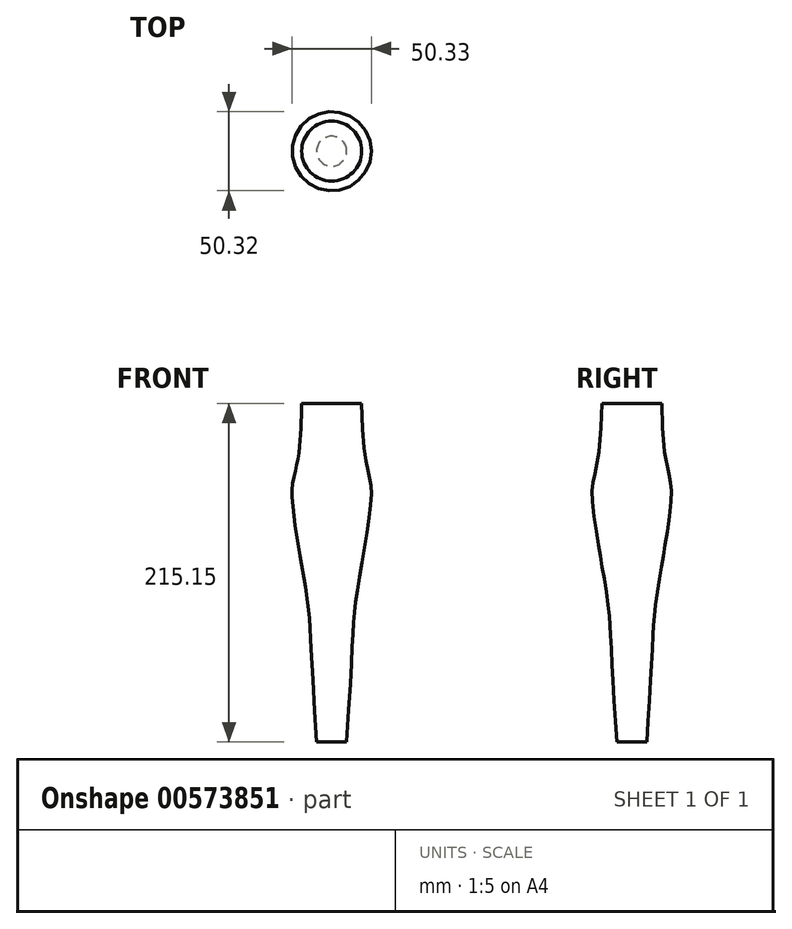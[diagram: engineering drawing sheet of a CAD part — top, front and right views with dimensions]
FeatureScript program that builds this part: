
annotation { "Feature Type Name" : "Feature", "Feature Type Description" : "" }
export const myFeature = defineFeature(function(context is Context, id is Id, definition is map)
    precondition{}
    {
        {
            var Q0;
            Q0=qCreatedBy(makeId("Front.planeOp"),FACE);
            var sketch = newSketch(context, id + "F0", { "sketchPlane" : qUnion([Q0])});
            skFitSpline(sketch, "E0", {"points": [v(0, 0) * mm, v(21.03, -44.85) * mm, v(13.62, -114.68) * mm, v(0, -231.47) * mm], "startDerivative": vector(0, -312.27) * mm, "endDerivative": vector(0, -470.96) * mm});
            skLineSegment(sketch, "E1", {"start": v(-209.5, -8.3) * mm, "end": v(-209.5, -223.46) * mm});
            skLineSegment(sketch, "E2", {"start": v(-209.5, -223.46) * mm, "end": v(-199.98, -223.46) * mm});
            skLineSegment(sketch, "E3", {"start": v(-190.46, -8.3) * mm, "end": v(-209.5, -8.3) * mm});
            skFitSpline(sketch, "E4", {"points": [v(-190.46, -8.3) * mm, v(-184.34, -65.02) * mm, v(-193.35, -128.04) * mm, v(-199.98, -223.46) * mm], "startDerivative": vector(4.3, -437.95) * mm, "endDerivative": vector(-35.6, -520.04) * mm});
            skSolve(sketch);
        }
        {
            var Q0;
            {var subQ0=sQuery(id+"F0.wireOp",EDGE,"E1");Q0=makeQuery(id+"F0.imprint","IMPRINT",FACE,{"disambiguationData":[TD([[makeQuery(id+"F0.imprint","IMPRINT",EDGE,{"derivedFrom":subQ0}),1.0]])]});}
            var Q1;
            Q1=sQuery(id+"F0.wireOp",EDGE,"E1");
            revolve(context, id + "F1", {"entities" : qUnion([Q0]), "axis" : qUnion([Q1]), "revolveType" : RevolveType.FULL});
        }
    });
